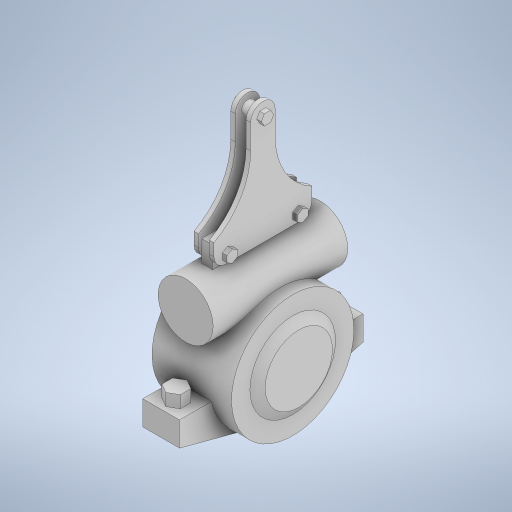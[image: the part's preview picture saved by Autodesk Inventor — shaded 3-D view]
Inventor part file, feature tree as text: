
AUTODESK INVENTOR PART (.ipt)
format: ipt  version: 2023 (Build 270158000, 158)  size: 466,432 bytes
history: native  units: in
note: dims shown in document units (in); Inventor stores cm internally (conversion verified against a paired STEP export)
features: extrude x7, sketch x7, mirror x2, revolve x1
ambient origin geometry x8: Origin, YZ Plane, XZ Plane, XY Plane, X Axis, Y Axis, Z Axis, Center Point
bodies: Solid1 (feature_tree)
feature tree (17):
  revolve  "Revolution1"  [1 undecoded]
  extrude  "Extrusion1"  TaperAngle=90.0deg  [1 undecoded]
  extrude  "Extrusion2"  Depth=1.5in
  extrude  "Extrusion3"  Depth=11.0in TaperAngle=0.0deg
  extrude  "Extrusion4"  Depth=1.0in
  extrude  "Extrusion5"  Depth=4.0in
  mirror  "Mirror1"
  extrude  "Extrusion6"  Depth=3.0in TaperAngle=0.0deg
  extrude  "Extrusion7"  Depth=2.0in
  mirror  "Mirror2"
  sketch  "Sketch1"  dims[d0=5.0in d1=6.5in]
  sketch  "Sketch2"  dims[d2=7.0in d3=90.0deg]
  sketch  "Sketch3"  dims[d4=1.5in d5=2.75in]
  sketch  "Sketch4"  dims[d6=4.5in d7=11.0in d8=0.0in]
  sketch  "Sketch5"  dims[d9=0.0in d10=1.0in]
  sketch  "Sketch7"  dims[d11=7.5in d12=4.0in]
  sketch  "Sketch8"  dims[d13=2.0in d14=3.0in d15=0.0in d16=2.0in d17=1.75in d18=2.0in d19=1.75in d20=0.875in d21=0.0in d22=0.0in d23=0.0in d24=0.2in d25=2.0in d26=7.0in d27=2.0in d28=9.0in d29=8.0in d30=0.375in d31=0.0in d32=1.0in d37=0.375in d38=0.0in d43=1.0in d44=1.0in d45=0.0in d46=0.875in d47=0.904in d48=0.875in d49=0.875in d50=0.875in d51=1.25in d52=1.5in d53=1.5in d54=1.0in d55=0.0in]
note: 2 required parameter values undecoded (feature->parameter linkage not recoverable at this tier; creation-order binding heuristic only, values carry confidence <= 0.55)